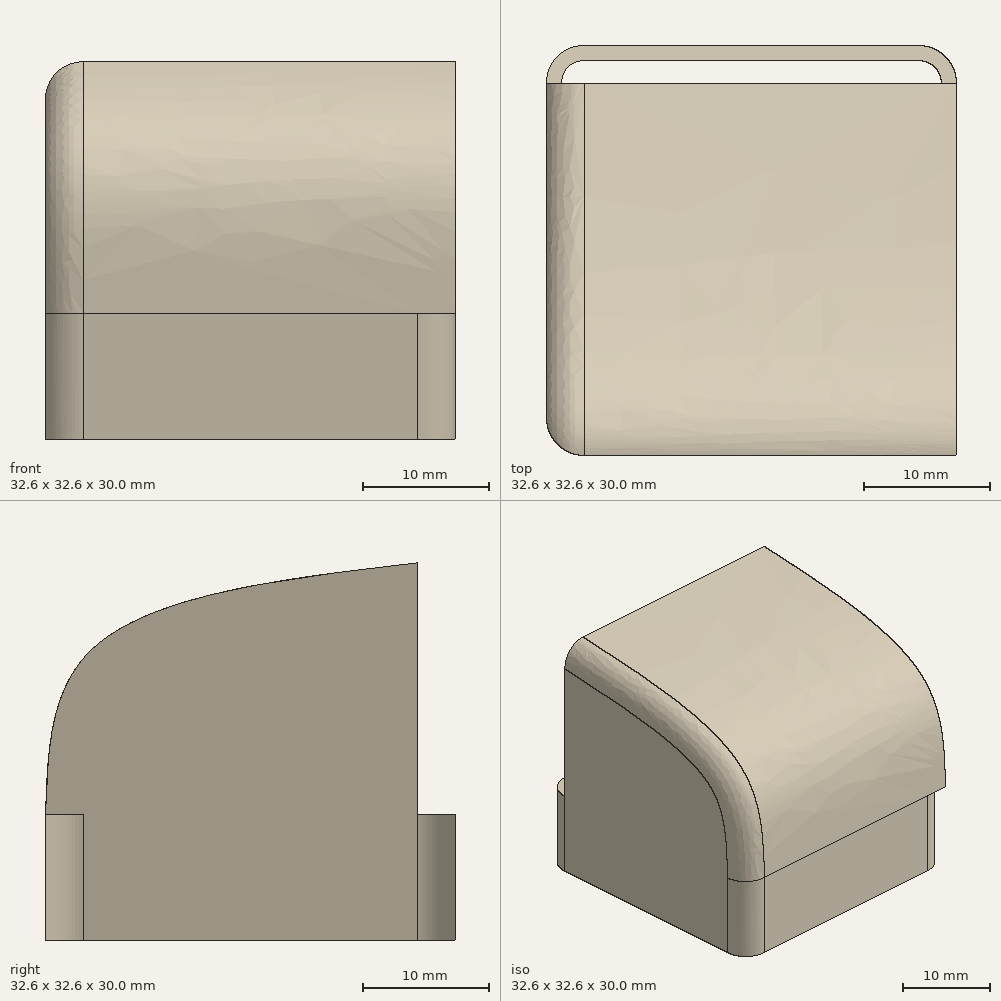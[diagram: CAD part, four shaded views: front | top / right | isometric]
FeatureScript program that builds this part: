
annotation { "Feature Type Name" : "Feature", "Feature Type Description" : "" }
export const myFeature = defineFeature(function(context is Context, id is Id, definition is map)
    precondition{}
    {
        {
            var Q0;
            Q0=qCreatedBy(makeId("Top.planeOp"),FACE);
            var sketch = newSketch(context, id + "F0", { "sketchPlane" : qUnion([Q0])});
            skLineSegment(sketch, "E0.bottom", {"start": v(16.3, -16.3) * mm, "end": v(-16.3, -16.3) * mm});
            skLineSegment(sketch, "E0.top", {"start": v(16.3, 16.3) * mm, "end": v(-16.3, 16.3) * mm});
            skLineSegment(sketch, "E0.left", {"start": v(16.3, -16.3) * mm, "end": v(16.3, 16.3) * mm});
            skLineSegment(sketch, "E0.right", {"start": v(-16.3, -16.3) * mm, "end": v(-16.3, 16.3) * mm});
            skPoint(sketch, "E0.middle", {"position": v(0, 0) * mm});
            skSolve(sketch);
        }
        {
            var Q0;
            Q0 = qSketchRegion(id + "F0", true);
            extrude(context, id + "F1", {"entities" : qUnion([Q0]), "depth" : 10 * mm});
        }
        {
            var Q0;
            Q0=makeQuery(id+"F1.opExtrude","SWEPT_EDGE",EDGE,{"disambiguationData":[OSD([sQuery(id+"F0.wireOp",EDGE,"E0.bottom"),sQuery(id+"F0.wireOp",EDGE,"E0.left")])]});
            var Q1;
            Q1=makeQuery(id+"F1.opExtrude","SWEPT_EDGE",EDGE,{"disambiguationData":[OSD([sQuery(id+"F0.wireOp",EDGE,"E0.bottom"),sQuery(id+"F0.wireOp",EDGE,"E0.right")])]});
            var Q2;
            Q2=makeQuery(id+"F1.opExtrude","SWEPT_EDGE",EDGE,{"disambiguationData":[OSD([sQuery(id+"F0.wireOp",EDGE,"E0.top"),sQuery(id+"F0.wireOp",EDGE,"E0.right")])]});
            var Q3;
            Q3=makeQuery(id+"F1.opExtrude","SWEPT_EDGE",EDGE,{"disambiguationData":[OSD([sQuery(id+"F0.wireOp",EDGE,"E0.top"),sQuery(id+"F0.wireOp",EDGE,"E0.left")])]});
            fillet(context, id + "F2", {"entities" : qUnion([Q0, Q1, Q2, Q3]), "radius" : 3 * mm, "tangentPropagation" : true, "allowEdgeOverflow" : false});
        }
        {
            var Q0;
            Q0=makeQuery(id+"F1.opExtrude","CAP_FACE",FACE,{"disambiguationData":[OSD([sQuery(id+"F0.wireOp",EDGE,"E0.bottom"),sQuery(id+"F0.wireOp",EDGE,"E0.top"),sQuery(id+"F0.wireOp",EDGE,"E0.left"),sQuery(id+"F0.wireOp",EDGE,"E0.right")])],"isStart":false});
            var Q1;
            Q1=makeQuery(id+"F1.opExtrude","CAP_FACE",FACE,{"disambiguationData":[OSD([sQuery(id+"F0.wireOp",EDGE,"E0.bottom"),sQuery(id+"F0.wireOp",EDGE,"E0.top"),sQuery(id+"F0.wireOp",EDGE,"E0.left"),sQuery(id+"F0.wireOp",EDGE,"E0.right")])],"isStart":true});
            shell(context, id + "F3", {"entities" : qUnion([Q0, Q1]), "thickness" : 1.2 * mm});
        }
        {
            var Q0;
            Q0=makeQuery(id+"F1.opExtrude","CAP_FACE",FACE,{"disambiguationData":[OSD([sQuery(id+"F0.wireOp",EDGE,"E0.bottom"),sQuery(id+"F0.wireOp",EDGE,"E0.top"),sQuery(id+"F0.wireOp",EDGE,"E0.left"),sQuery(id+"F0.wireOp",EDGE,"E0.right")])],"isStart":false});
            var sketch = newSketch(context, id + "F4", { "sketchPlane" : qUnion([Q0])});
            skLineSegment(sketch, "E1", {"start": v(0, -16.3) * mm, "end": v(22.5, -16.3) * mm, "construction": true});
            skLineSegment(sketch, "E2", {"start": v(0, -16.3) * mm, "end": v(-17.96, -16.3) * mm, "construction": true});
            skLineSegment(sketch, "E3", {"start": v(-16.3, 0) * mm, "end": v(-16.3, -16.3) * mm, "construction": true});
            skLineSegment(sketch, "E4", {"start": v(16.3, 0) * mm, "end": v(16.3, -16.3) * mm, "construction": true});
            skLineSegment(sketch, "E5.bottom", {"start": v(-16.3, 13.3) * mm, "end": v(16.3, 13.3) * mm});
            skLineSegment(sketch, "E5.top", {"start": v(-16.3, -16.3) * mm, "end": v(16.3, -16.3) * mm});
            skLineSegment(sketch, "E5.left", {"start": v(-16.3, 13.3) * mm, "end": v(-16.3, -16.3) * mm});
            skLineSegment(sketch, "E5.right", {"start": v(16.3, 13.3) * mm, "end": v(16.3, -16.3) * mm});
            skSolve(sketch);
        }
        {
            var Q0;
            Q0 = qSketchRegion(id + "F4", true);
            extrude(context, id + "F5", {"entities" : qUnion([Q0]), "operationType" : NewBodyOperationType.ADD, "depth" : 20 * mm});
        }
        {
            var Q0;
            Q0=makeQuery(id+"F5.boolean.opBoolean","MERGE",FACE,{"derivedFrom":[makeQuery(id+"F1.opExtrude","SWEPT_FACE",FACE,{"disambiguationData":[OSD([sQuery(id+"F0.wireOp",EDGE,"E0.left")])]}),makeQuery(id+"F5.opExtrude","SWEPT_FACE",FACE,{"disambiguationData":[OSD([sQuery(id+"F4.wireOp",EDGE,"E5.right")])]})]});
            var sketch = newSketch(context, id + "F6", { "sketchPlane" : qUnion([Q0])});
            skFitSpline(sketch, "E6", {"points": [v(-16.3, 10) * mm, v(-12.77, 22.94) * mm, v(13.3, 30) * mm], "startDerivative": vector(1.13, 35.28) * mm, "endDerivative": vector(54.96, 6.39) * mm});
            skLineSegment(sketch, "E7", {"start": v(13.3, 30) * mm, "end": v(-16.3, 30) * mm});
            skLineSegment(sketch, "E8", {"start": v(-16.3, 30) * mm, "end": v(-16.3, 10) * mm});
            skSolve(sketch);
        }
        {
            var Q0;
            Q0=makeQuery(id+"F6.imprint","IMPRINT",FACE,{"disambiguationData":[TD([[makeQuery(id+"F6.imprint","IMPRINT",EDGE,{"derivedFrom":sQuery(id+"F6.wireOp",EDGE,"E6")}),1.0]])]});
            extrude(context, id + "F7", {"entities" : qUnion([Q0]), "operationType" : NewBodyOperationType.REMOVE, "endBound" : BoundingType.THROUGH_ALL, "oppositeDirection" : true, "depth" : 25 * mm});
        }
        {
            var Q0;
            Q0=makeQuery(id+"F7.boolean.opBoolean","COPY",EDGE,{"derivedFrom":makeQuery(id+"F7.opExtrude","CAP_EDGE",EDGE,{"disambiguationData":[OSD([sQuery(id+"F6.wireOp",EDGE,"E6")])],"isStart":true})});
            var Q1;
            Q1=makeQuery(id+"F7.boolean.opBoolean","INTERSECT",EDGE,{"derivedFrom":[makeQuery(id+"F5.boolean.opBoolean","MERGE",FACE,{"derivedFrom":[makeQuery(id+"F1.opExtrude","SWEPT_FACE",FACE,{"disambiguationData":[OSD([sQuery(id+"F0.wireOp",EDGE,"E0.right")])]}),makeQuery(id+"F5.opExtrude","SWEPT_FACE",FACE,{"disambiguationData":[OSD([sQuery(id+"F4.wireOp",EDGE,"E5.left")])]})]}),makeQuery(id+"F7.opExtrude","SWEPT_FACE",FACE,{"disambiguationData":[OSD([sQuery(id+"F6.wireOp",EDGE,"E6")])]})]});
            fillet(context, id + "F8", {"entities" : qUnion([Q0, Q1]), "radius" : 3 * mm, "tangentPropagation" : true, "allowEdgeOverflow" : false});
        }
        {
            var Q0;
            Q0=makeQuery(id+"F5.opExtrude","SWEPT_FACE",FACE,{"disambiguationData":[OSD([sQuery(id+"F4.wireOp",EDGE,"E5.bottom")])]});
            var Q1;
            {var subQ3=sQuery(id+"F0.wireOp",EDGE,"E0.bottom");var subQ4=sQuery(id+"F4.wireOp",EDGE,"E5.bottom");Q1=makeQuery(id+"F5.boolean.opBoolean","SPLIT",FACE,{"disambiguationData":[TD([makeQuery(id+"F3.opShell","OFFSET_FACE",FACE,{"disambiguationData":[OSD([subQ3])]})])],"derivedFrom":makeQuery(id+"F5.opExtrude","CAP_FACE",FACE,{"disambiguationData":[OSD([subQ4,sQuery(id+"F4.wireOp",EDGE,"E5.top"),sQuery(id+"F4.wireOp",EDGE,"E5.left"),sQuery(id+"F4.wireOp",EDGE,"E5.right")])],"isStart":true})});}
            shell(context, id + "F9", {"entities" : qUnion([Q0, Q1]), "thickness" : 1.2 * mm});
        }
    });
